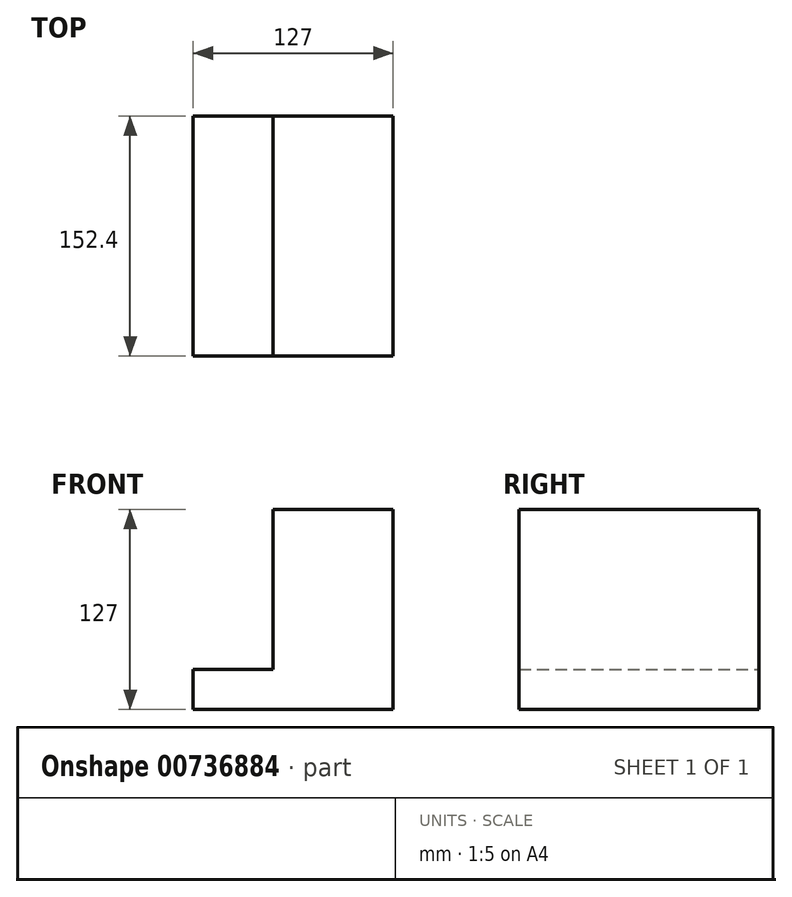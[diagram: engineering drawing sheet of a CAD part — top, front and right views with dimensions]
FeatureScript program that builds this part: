
annotation { "Feature Type Name" : "Feature", "Feature Type Description" : "" }
export const myFeature = defineFeature(function(context is Context, id is Id, definition is map)
    precondition{}
    {
        {
            var Q0;
            Q0=qCreatedBy(makeId("Front.planeOp"),FACE);
            var sketch = newSketch(context, id + "F0", { "sketchPlane" : qUnion([Q0])});
            skLineSegment(sketch, "E0", {"start": v(-75.48, -39.86) * mm, "end": v(51.52, -39.86) * mm});
            skLineSegment(sketch, "E1", {"start": v(51.52, -39.86) * mm, "end": v(51.52, 87.14) * mm});
            skLineSegment(sketch, "E2", {"start": v(51.52, 87.14) * mm, "end": v(-24.68, 87.14) * mm});
            skLineSegment(sketch, "E3", {"start": v(-24.68, 87.14) * mm, "end": v(-24.68, -14.46) * mm});
            skLineSegment(sketch, "E4", {"start": v(-24.68, -14.46) * mm, "end": v(-75.48, -14.46) * mm});
            skLineSegment(sketch, "E5", {"start": v(-75.48, -14.46) * mm, "end": v(-75.48, -39.86) * mm});
            skSolve(sketch);
        }
        {
            var Q0;
            Q0=makeQuery(id+"F0.imprint","IMPRINT",FACE,{"disambiguationData":[TD([[makeQuery(id+"F0.imprint","IMPRINT",EDGE,{"derivedFrom":sQuery(id+"F0.wireOp",EDGE,"E0")}),1.0]])]});
            extrude(context, id + "F1", {"entities" : qUnion([Q0]), "depth" : 152.4 * mm, "offsetDistance" : 25.4 * mm});
        }
    });
